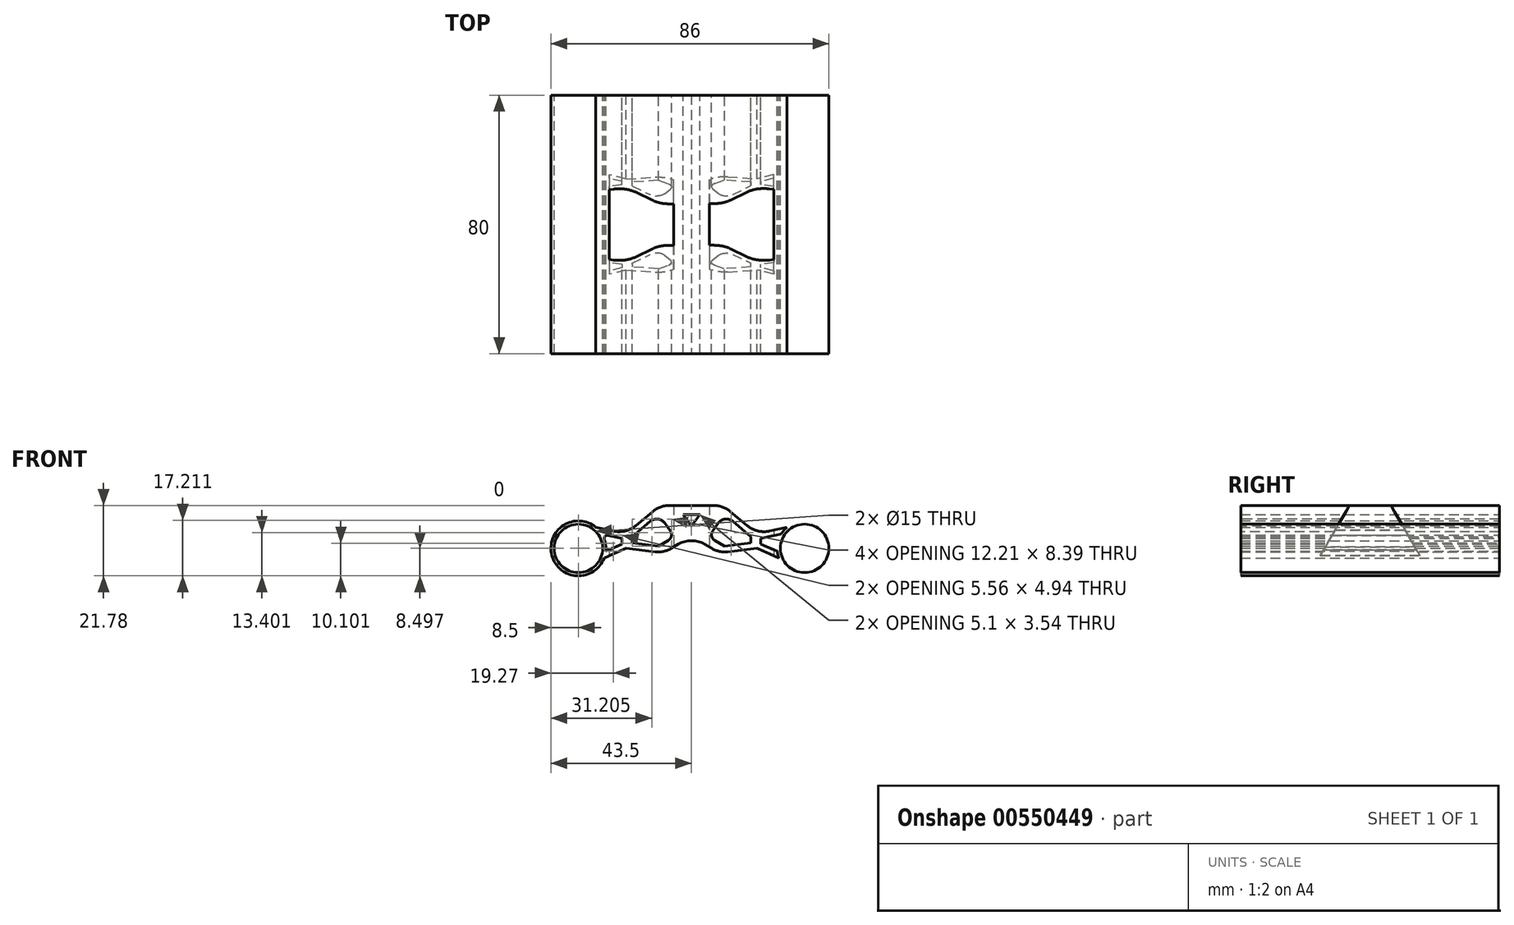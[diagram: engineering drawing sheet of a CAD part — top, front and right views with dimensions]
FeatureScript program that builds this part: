
annotation { "Feature Type Name" : "Feature", "Feature Type Description" : "" }
export const myFeature = defineFeature(function(context is Context, id is Id, definition is map)
    precondition{}
    {
        {
            var Q0;
            Q0=qCreatedBy(makeId("Front.planeOp"),FACE);
            var sketch = newSketch(context, id + "F0", { "sketchPlane" : qUnion([Q0])});
            skCircle(sketch, "E0.MirrorC", {"center": v(-35, -3.62) * mm, "radius": 7.5 * mm});
            skLineSegment(sketch, "E1.MirrorCS", {"start": v(-21.45, -2.26) * mm, "end": v(-26.54, -4.49) * mm});
            skLineSegment(sketch, "E2.MirrorCS", {"start": v(-21.45, -0.52) * mm, "end": v(-21.45, -2.26) * mm});
            skLineSegment(sketch, "E3.MirrorCS", {"start": v(-20.25, -3.62) * mm, "end": v(-27.03, -6.58) * mm});
            skLineSegment(sketch, "E4.MirrorCS", {"start": v(-9.82, 9.66) * mm, "end": v(-20.25, 0.9) * mm});
            skPoint(sketch, "E5.MirrorP", {"position": v(-30.62, -8.15) * mm});
            skPoint(sketch, "E6.MirrorP", {"position": v(-4.28, -2.47) * mm});
            skCircle(sketch, "E7.MirrorC", {"center": v(-35, -3.62) * mm, "radius": 8.5 * mm});
            skLineSegment(sketch, "E8.MirrorCS", {"start": v(-20.25, 0.9) * mm, "end": v(-29.59, 2.93) * mm});
            skLineSegment(sketch, "E9.MirrorCS", {"start": v(-21.45, -0.52) * mm, "end": v(-27.78, 0.86) * mm});
            skLineSegment(sketch, "E10.MirrorCS", {"start": v(-20.25, -3.62) * mm, "end": v(-8.55, -4.99) * mm});
            skPoint(sketch, "E11.MirrorP", {"position": v(-41.25, -2.83) * mm});
            skLineSegment(sketch, "E12.MirrorCS", {"start": v(-8.55, -4.99) * mm, "end": v(0, 0.05) * mm});
            skLineSegment(sketch, "E13", {"start": v(-10.23, -2.91) * mm, "end": v(-18.4, -1.96) * mm});
            skLineSegment(sketch, "E14", {"start": v(-18.4, 0.01) * mm, "end": v(-18.4, -1.96) * mm});
            skCircle(sketch, "E15.MirrorC", {"center": v(35, -3.62) * mm, "radius": 7.5 * mm});
            skPoint(sketch, "E16.MirrorP", {"position": v(4.28, -2.47) * mm});
            skLineSegment(sketch, "E17.MirrorCS", {"start": v(21.45, -2.27) * mm, "end": v(26.54, -4.49) * mm});
            skPoint(sketch, "E18.MirrorP", {"position": v(41.25, -2.83) * mm});
            skLineSegment(sketch, "E19.MirrorCS", {"start": v(21.45, -0.52) * mm, "end": v(21.45, -2.27) * mm});
            skLineSegment(sketch, "E20.MirrorCS", {"start": v(20.25, -3.62) * mm, "end": v(27.03, -6.58) * mm});
            skLineSegment(sketch, "E21.MirrorCS", {"start": v(9.82, 9.66) * mm, "end": v(20.25, 0.9) * mm});
            skCircle(sketch, "E22.MirrorC", {"center": v(35, -3.62) * mm, "radius": 8.5 * mm});
            skLineSegment(sketch, "E23.MirrorCS", {"start": v(20.25, 0.9) * mm, "end": v(29.59, 2.93) * mm});
            skLineSegment(sketch, "E24.MirrorCS", {"start": v(21.45, -0.52) * mm, "end": v(27.78, 0.86) * mm});
            skLineSegment(sketch, "E25.MirrorCS", {"start": v(20.25, -3.62) * mm, "end": v(8.55, -4.99) * mm});
            skPoint(sketch, "E26.MirrorP", {"position": v(30.62, -8.15) * mm});
            skLineSegment(sketch, "E27.MirrorCS", {"start": v(8.55, -4.99) * mm, "end": v(0, 0.05) * mm});
            skLineSegment(sketch, "E28", {"start": v(-9.82, 9.66) * mm, "end": v(9.82, 9.66) * mm});
            skLineSegment(sketch, "E29", {"start": v(-10.23, -2.91) * mm, "end": v(-5.29, 0) * mm});
            skLineSegment(sketch, "E30", {"start": v(-18.4, 0.01) * mm, "end": v(-10.23, 6.86) * mm});
            skLineSegment(sketch, "E31", {"start": v(-10.23, 6.86) * mm, "end": v(-5.29, 0) * mm});
            skLineSegment(sketch, "E32", {"start": v(0, 3.32) * mm, "end": v(-2.55, 6.86) * mm});
            skLineSegment(sketch, "E33.MirrorCS", {"start": v(0, 3.32) * mm, "end": v(2.55, 6.86) * mm});
            skLineSegment(sketch, "E34", {"start": v(-2.55, 6.86) * mm, "end": v(2.55, 6.86) * mm});
            skLineSegment(sketch, "E35.MirrorCS", {"start": v(10.23, 6.86) * mm, "end": v(5.29, 0) * mm});
            skLineSegment(sketch, "E36.MirrorCS", {"start": v(18.4, 0.01) * mm, "end": v(10.23, 6.86) * mm});
            skLineSegment(sketch, "E37.MirrorCS", {"start": v(18.4, 0.01) * mm, "end": v(18.4, -1.96) * mm});
            skLineSegment(sketch, "E38.MirrorCS", {"start": v(10.23, -2.91) * mm, "end": v(18.4, -1.96) * mm});
            skLineSegment(sketch, "E39.MirrorCS", {"start": v(10.23, -2.91) * mm, "end": v(5.29, 0) * mm});
            skSolve(sketch);
        }
        {
            var Q0;
            {var subQ3=sQuery(id+"F0.wireOp",EDGE,"E1.MirrorCS");Q0=makeQuery(id+"F0.imprint","IMPRINT",FACE,{"disambiguationData":[TD([[makeQuery(id+"F0.imprint","IMPRINT",EDGE,{"derivedFrom":subQ3}),1.0]])]});}
            var Q1;
            Q1=makeQuery(id+"F0.imprint","IMPRINT",FACE,{"disambiguationData":[TD([[makeQuery(id+"F0.imprint","IMPRINT",EDGE,{"derivedFrom":sQuery(id+"F0.wireOp",EDGE,"E0.MirrorC")}),-1.0]])]});
            var Q2;
            Q2=makeQuery(id+"F0.imprint","IMPRINT",FACE,{"disambiguationData":[TD([[makeQuery(id+"F0.imprint","IMPRINT",EDGE,{"derivedFrom":sQuery(id+"F0.wireOp",EDGE,"E15.MirrorC")}),1.0]])]});
            extrude(context, id + "F1", {"entities" : qUnion([Q0, Q1, Q2]), "depth" : 80 * mm, "offsetDistance" : 25 * mm});
        }
        {
            var Q0;
            Q0=makeQuery(id+"F1.opExtrude","SWEPT_EDGE",EDGE,{"disambiguationData":[OSD([sQuery(id+"F0.wireOp",EDGE,"E4.MirrorCS"),sQuery(id+"F0.wireOp",EDGE,"E28")])]});
            var Q1;
            Q1=makeQuery(id+"F1.opExtrude","SWEPT_EDGE",EDGE,{"disambiguationData":[OSD([sQuery(id+"F0.wireOp",EDGE,"E21.MirrorCS"),sQuery(id+"F0.wireOp",EDGE,"E28")])]});
            var Q2;
            Q2=makeQuery(id+"F1.opExtrude","SWEPT_EDGE",EDGE,{"disambiguationData":[OSD([sQuery(id+"F0.wireOp",EDGE,"E4.MirrorCS"),sQuery(id+"F0.wireOp",EDGE,"E8.MirrorCS")])]});
            var Q3;
            Q3=makeQuery(id+"F1.opExtrude","SWEPT_EDGE",EDGE,{"disambiguationData":[OSD([sQuery(id+"F0.wireOp",EDGE,"E21.MirrorCS"),sQuery(id+"F0.wireOp",EDGE,"E23.MirrorCS")])]});
            var Q4;
            Q4=makeQuery(id+"F1.opExtrude","SWEPT_EDGE",EDGE,{"disambiguationData":[OSD([sQuery(id+"F0.wireOp",EDGE,"E12.MirrorCS"),sQuery(id+"F0.wireOp",EDGE,"E27.MirrorCS")])]});
            var Q5;
            Q5=makeQuery(id+"F1.opExtrude","SWEPT_EDGE",EDGE,{"disambiguationData":[OSD([sQuery(id+"F0.wireOp",EDGE,"E10.MirrorCS"),sQuery(id+"F0.wireOp",EDGE,"E12.MirrorCS")])]});
            var Q6;
            Q6=makeQuery(id+"F1.opExtrude","SWEPT_EDGE",EDGE,{"disambiguationData":[OSD([sQuery(id+"F0.wireOp",EDGE,"E25.MirrorCS"),sQuery(id+"F0.wireOp",EDGE,"E27.MirrorCS")])]});
            fillet(context, id + "F2", {"entities" : qUnion([Q0, Q1, Q2, Q3, Q4, Q5, Q6]), "radius" : 8 * mm, "tangentPropagation" : true, "allowEdgeOverflow" : false});
        }
        {
            var Q0;
            Q0=makeQuery(id+"F1.opExtrude","SWEPT_EDGE",EDGE,{"disambiguationData":[OSD([sQuery(id+"F0.wireOp",EDGE,"E30"),sQuery(id+"F0.wireOp",EDGE,"E31")])]});
            var Q1;
            Q1=makeQuery(id+"F1.opExtrude","SWEPT_EDGE",EDGE,{"disambiguationData":[OSD([sQuery(id+"F0.wireOp",EDGE,"E36.MirrorCS"),sQuery(id+"F0.wireOp",EDGE,"E35.MirrorCS")])]});
            fillet(context, id + "F3", {"entities" : qUnion([Q0, Q1]), "radius" : 3 * mm, "tangentPropagation" : true, "allowEdgeOverflow" : false});
        }
        {
            var Q0;
            Q0=makeQuery(id+"F1.opExtrude","SWEPT_EDGE",EDGE,{"disambiguationData":[OSD([sQuery(id+"F0.wireOp",EDGE,"E7.MirrorC"),sQuery(id+"F0.wireOp",EDGE,"E9.MirrorCS")])]});
            var Q1;
            Q1=makeQuery(id+"F1.opExtrude","SWEPT_EDGE",EDGE,{"disambiguationData":[OSD([sQuery(id+"F0.wireOp",EDGE,"E22.MirrorC"),sQuery(id+"F0.wireOp",EDGE,"E24.MirrorCS")])]});
            fillet(context, id + "F4", {"entities" : qUnion([Q0, Q1]), "radius" : 1 * mm, "tangentPropagation" : true, "allowEdgeOverflow" : false});
        }
        {
            var Q0;
            Q0=qCreatedBy(makeId("Right.planeOp"),FACE);
            cPlane(context, id + "F5", {"entities" : qUnion([Q0]), "cplaneType" : CPlaneType.OFFSET, "offset" : 5.5 * mm, "oppositeDirection" : true, "width" : 150 * mm, "height" : 150 * mm});
        }
        {
            var Q0;
            Q0=makeQuery(id+"F1.opExtrude","SWEPT_EDGE",EDGE,{"disambiguationData":[OSD([sQuery(id+"F0.wireOp",EDGE,"E39.MirrorCS"),sQuery(id+"F0.wireOp",EDGE,"E35.MirrorCS")])]});
            var Q1;
            Q1=makeQuery(id+"F1.opExtrude","SWEPT_EDGE",EDGE,{"disambiguationData":[OSD([sQuery(id+"F0.wireOp",EDGE,"E29"),sQuery(id+"F0.wireOp",EDGE,"E31")])]});
            fillet(context, id + "F6", {"entities" : qUnion([Q0, Q1]), "radius" : 2 * mm, "tangentPropagation" : true, "allowEdgeOverflow" : false});
        }
        {
            var Q0;
            Q0=qCreatedBy(id+"F5.planeOp",FACE);
            var sketch = newSketch(context, id + "F7", { "sketchPlane" : qUnion([Q0])});
            skLineSegment(sketch, "E40", {"start": v(-0.04, 9.77) * mm, "end": v(-80.04, 9.77) * mm});
            skLineSegment(sketch, "E41", {"start": v(-40.04, 9.77) * mm, "end": v(-40.04, 20.76) * mm});
            skLineSegment(sketch, "E42", {"start": v(-40.04, 20.76) * mm, "end": v(-15.04, -22.54) * mm});
            skLineSegment(sketch, "E43", {"start": v(-40.04, 20.76) * mm, "end": v(-65.04, -22.54) * mm});
            skLineSegment(sketch, "E44", {"start": v(-15.04, -22.54) * mm, "end": v(-65.04, -22.54) * mm});
            skSolve(sketch);
        }
        {
            var Q0;
            Q0=qCreatedBy(makeId("Right.planeOp"),FACE);
            cPlane(context, id + "F8", {"entities" : qUnion([Q0]), "cplaneType" : CPlaneType.OFFSET, "offset" : 5.5 * mm, "width" : 150 * mm, "height" : 150 * mm});
        }
        {
            var Q0;
            Q0=qCreatedBy(id+"F8.planeOp",FACE);
            var sketch = newSketch(context, id + "F9", { "sketchPlane" : qUnion([Q0])});
            skLineSegment(sketch, "E45", {"start": v(0, 9.83) * mm, "end": v(-80, 9.83) * mm});
            skLineSegment(sketch, "E46", {"start": v(-40, 9.83) * mm, "end": v(-40, 20.82) * mm});
            skLineSegment(sketch, "E47", {"start": v(-40, 20.82) * mm, "end": v(-15, -22.48) * mm});
            skLineSegment(sketch, "E48", {"start": v(-40, 20.82) * mm, "end": v(-65, -22.48) * mm});
            skLineSegment(sketch, "E49", {"start": v(-15, -22.48) * mm, "end": v(-65, -22.48) * mm});
            skSolve(sketch);
        }
        {
            var Q0;
            {var subQ0=sQuery(id+"F7.wireOp",EDGE,"E41");Q0=makeQuery(id+"F7.imprint","IMPRINT",FACE,{"disambiguationData":[TD([[makeQuery(id+"F7.imprint","IMPRINT",EDGE,{"derivedFrom":subQ0}),-1.0]])]});}
            var Q1;
            {var subQ0=sQuery(id+"F7.wireOp",EDGE,"E41");Q1=makeQuery(id+"F7.imprint","IMPRINT",FACE,{"disambiguationData":[TD([[makeQuery(id+"F7.imprint","IMPRINT",EDGE,{"derivedFrom":subQ0}),1.0]])]});}
            var Q2;
            {var subQ0=sQuery(id+"F7.wireOp",EDGE,"E44");Q2=makeQuery(id+"F7.imprint","IMPRINT",FACE,{"disambiguationData":[TD([[makeQuery(id+"F7.imprint","IMPRINT",EDGE,{"derivedFrom":subQ0}),-1.0]])]});}
            extrude(context, id + "F10", {"entities" : qUnion([Q0, Q1, Q2]), "operationType" : NewBodyOperationType.REMOVE, "oppositeDirection" : true, "depth" : 20 * mm, "offsetDistance" : 25 * mm});
        }
        {
            var Q0;
            {var subQ0=sQuery(id+"F9.wireOp",EDGE,"E49");Q0=makeQuery(id+"F9.imprint","IMPRINT",FACE,{"disambiguationData":[TD([[makeQuery(id+"F9.imprint","IMPRINT",EDGE,{"derivedFrom":subQ0}),-1.0]])]});}
            var Q1;
            {var subQ0=sQuery(id+"F9.wireOp",EDGE,"E46");Q1=makeQuery(id+"F9.imprint","IMPRINT",FACE,{"disambiguationData":[TD([[makeQuery(id+"F9.imprint","IMPRINT",EDGE,{"derivedFrom":subQ0}),-1.0]])]});}
            var Q2;
            {var subQ0=sQuery(id+"F9.wireOp",EDGE,"E46");Q2=makeQuery(id+"F9.imprint","IMPRINT",FACE,{"disambiguationData":[TD([[makeQuery(id+"F9.imprint","IMPRINT",EDGE,{"derivedFrom":subQ0}),1.0]])]});}
            extrude(context, id + "F11", {"entities" : qUnion([Q0, Q1, Q2]), "operationType" : NewBodyOperationType.REMOVE, "depth" : 20 * mm, "offsetDistance" : 25 * mm});
        }
    });
